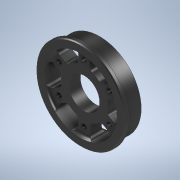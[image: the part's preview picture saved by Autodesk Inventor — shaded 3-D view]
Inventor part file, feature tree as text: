
AUTODESK INVENTOR PART (.ipt)
format: ipt  version: 2020 (Build 240168000, 168)  size: 305,664 bytes
history: native  units: in
note: dims shown in document units (in); Inventor stores cm internally (conversion verified against a paired STEP export)
features: sketch x3, revolve x1, extrude x1, pattern_circular x1, fillet x1, hole x1, chamfer x1
ambient origin geometry x8: Origin, YZ Plane, XZ Plane, XY Plane, X Axis, Y Axis, Z Axis, Center Point
bodies: Solid1 (feature_tree)
feature tree (9):
  revolve  "Revolution1"  [1 undecoded]
  extrude  "Extrusion1"  Depth=0.125in
  pattern_circular  "Circular Pattern1"  [2 undecoded]
  fillet  "Fillet1"  Radius=1.5in
  hole  "Hole1"  [1 undecoded]
  chamfer  "Chamfer1"  Distance=0.1875in
  sketch  "Sketch1"  dims[d0=1.4375in d1=0.25in]
  sketch  "Sketch2"  dims[d2=1.343in d3=0.125in]
  sketch  "Sketch3"  dims[d4=90.0deg d5=1.0in d6=1.5in d7=60.0deg d8=0.1875in d9=0.1875in d10=0.0in d11=0.0in d12=0.5in d13=0.125in d14=2.3622in d15=360.0deg d17=0.125in d18=1.875in d19=2.3622in d21=360.0deg d23=0.17in d24=0.75in d25=0.51in d26=0.188in d27=0.5635in d28=1.0in d29=0.8108in d30=0.0312in d31=0.125in d32=45.0deg]
note: 4 required parameter values undecoded (feature->parameter linkage not recoverable at this tier; creation-order binding heuristic only, values carry confidence <= 0.55)